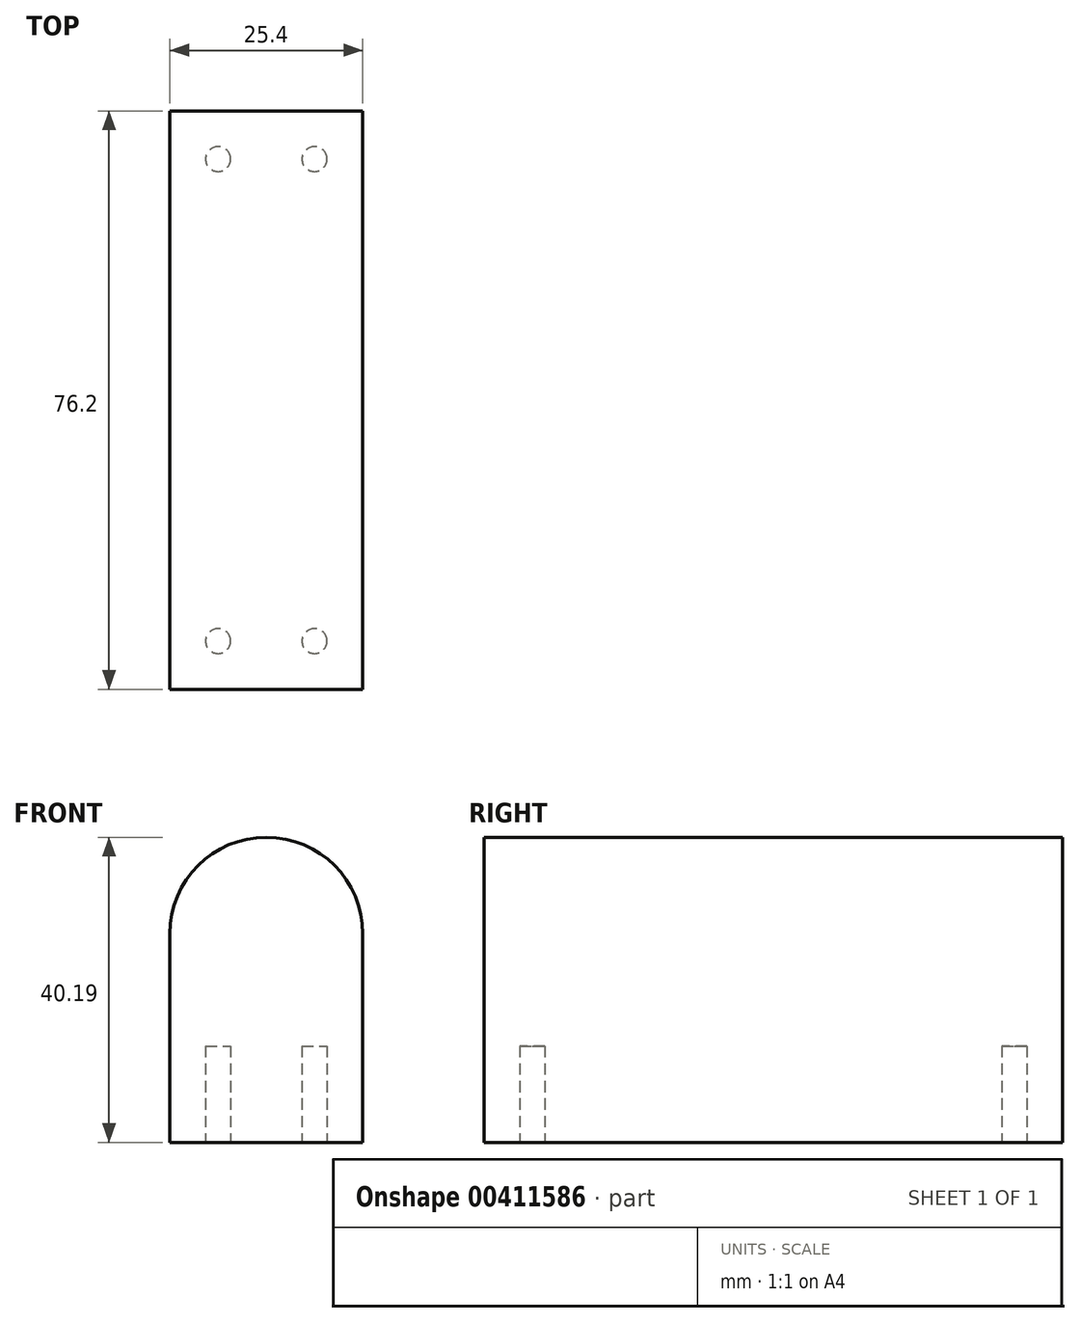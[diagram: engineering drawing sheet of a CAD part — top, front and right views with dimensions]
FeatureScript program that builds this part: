
annotation { "Feature Type Name" : "Feature", "Feature Type Description" : "" }
export const myFeature = defineFeature(function(context is Context, id is Id, definition is map)
    precondition{}
    {
        {
            var Q0;
            Q0=qCreatedBy(makeId("Front.planeOp"),FACE);
            var sketch = newSketch(context, id + "F0", { "sketchPlane" : qUnion([Q0])});
            skLineSegment(sketch, "E0", {"start": v(-16.78, 0) * mm, "end": v(8.62, 0) * mm});
            skArc(sketch, "E1", {"start": v(8.62, 27.5) * mm, "mid": v(-4.08, 40.2) * mm, "end": v(-16.78, 27.5) * mm});
            skPoint(sketch, "E1.centerSnap0", {"position": v(-4.08, 0) * mm});
            skCircle(sketch, "E2", {"center": v(-4.08, 27.5) * mm, "radius": 9.53 * mm});
            skLineSegment(sketch, "E3", {"start": v(-16.78, 0) * mm, "end": v(-16.78, 27.5) * mm});
            skLineSegment(sketch, "E4", {"start": v(8.62, 0) * mm, "end": v(8.62, 27.5) * mm});
            skSolve(sketch);
        }
        {
            var Q0;
            Q0=makeQuery(id+"F0.imprint","IMPRINT",FACE,{"disambiguationData":[TD([[makeQuery(id+"F0.imprint","IMPRINT",EDGE,{"derivedFrom":sQuery(id+"F0.wireOp",EDGE,"E2")}),1.0]])]});
            var Q1;
            Q1=makeQuery(id+"F0.imprint","IMPRINT",FACE,{"disambiguationData":[TD([[makeQuery(id+"F0.imprint","IMPRINT",EDGE,{"derivedFrom":sQuery(id+"F0.wireOp",EDGE,"E0")}),1.0]])]});
            extrude(context, id + "F1", {"entities" : qUnion([Q0, Q1]), "depth" : 76.2 * mm});
        }
        {
            var Q0;
            Q0=makeQuery(id+"F1.opExtrude","SWEPT_FACE",FACE,{"disambiguationData":[OSD([sQuery(id+"F0.wireOp",EDGE,"E0")])]});
            var sketch = newSketch(context, id + "F2", { "sketchPlane" : qUnion([Q0])});
            skCircle(sketch, "E5", {"center": v(-10.43, 6.35) * mm, "radius": 1.65 * mm});
            skCircle(sketch, "E6", {"center": v(-10.43, 69.85) * mm, "radius": 1.65 * mm});
            skCircle(sketch, "E7", {"center": v(2.27, 6.35) * mm, "radius": 1.65 * mm});
            skCircle(sketch, "E8", {"center": v(2.27, 69.85) * mm, "radius": 1.65 * mm});
            skSolve(sketch);
        }
        {
            var Q0;
            Q0 = qSketchRegion(id + "F2", true);
            extrude(context, id + "F3", {"entities" : qUnion([Q0]), "operationType" : NewBodyOperationType.REMOVE, "oppositeDirection" : true, "depth" : 12.7 * mm});
        }
    });
